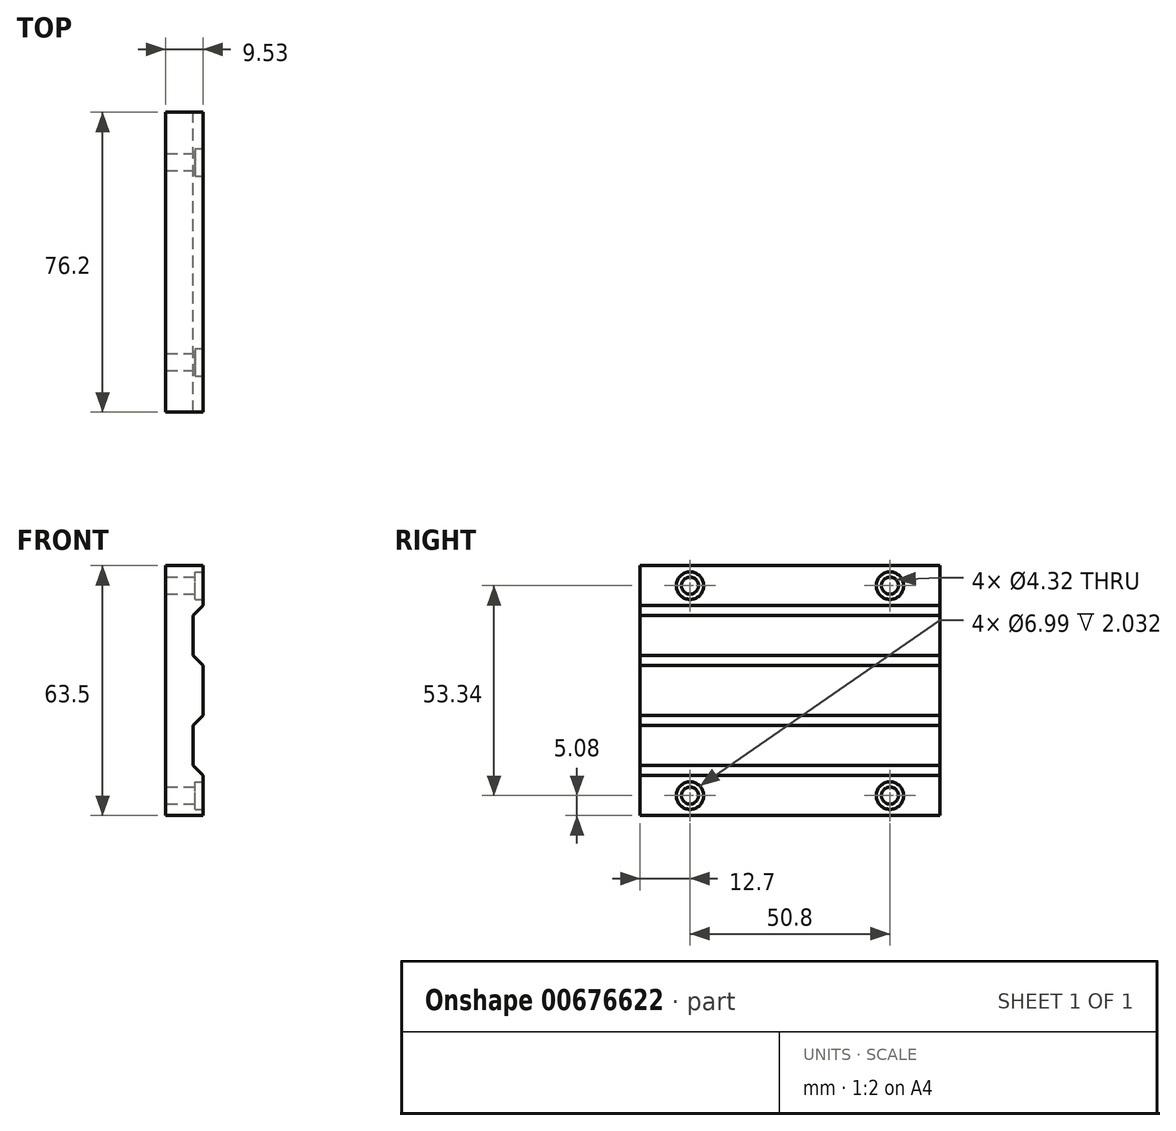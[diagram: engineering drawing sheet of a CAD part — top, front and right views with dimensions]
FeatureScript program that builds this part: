
annotation { "Feature Type Name" : "Feature", "Feature Type Description" : "" }
export const myFeature = defineFeature(function(context is Context, id is Id, definition is map)
    precondition{}
    {
        {
            var Q0;
            Q0=qCreatedBy(makeId("Front.planeOp"),FACE);
            var sketch = newSketch(context, id + "F0", { "sketchPlane" : qUnion([Q0])});
            skLineSegment(sketch, "E0.bottom", {"start": v(0, 0) * mm, "end": v(9.53, 0) * mm});
            skLineSegment(sketch, "E0.top", {"start": v(0, 63.5) * mm, "end": v(9.52, 63.5) * mm});
            skLineSegment(sketch, "E0.left", {"start": v(0, 0) * mm, "end": v(0, 63.5) * mm});
            skLineSegment(sketch, "E0.right", {"start": v(9.53, 0) * mm, "end": v(9.52, 63.5) * mm});
            skPoint(sketch, "E1.endSnap0", {"position": v(4.76, 63.5) * mm});
            skLineSegment(sketch, "E2", {"start": v(6.98, 50.8) * mm, "end": v(6.98, 40.64) * mm});
            skLineSegment(sketch, "E3", {"start": v(6.98, 40.64) * mm, "end": v(9.52, 38.1) * mm});
            skLineSegment(sketch, "E4", {"start": v(9.53, 25.4) * mm, "end": v(6.98, 22.86) * mm});
            skLineSegment(sketch, "E5", {"start": v(6.98, 22.86) * mm, "end": v(6.99, 12.7) * mm});
            skLineSegment(sketch, "E6", {"start": v(6.99, 12.7) * mm, "end": v(9.53, 10.16) * mm});
            skLineSegment(sketch, "E7", {"start": v(6.98, 50.8) * mm, "end": v(9.52, 53.34) * mm});
            skSolve(sketch);
        }
        {
            var Q0;
            {var subQ5=sQuery(id+"F0.wireOp",EDGE,"E0.bottom");Q0=makeQuery(id+"F0.imprint","IMPRINT",FACE,{"disambiguationData":[TD([[makeQuery(id+"F0.imprint","IMPRINT",EDGE,{"derivedFrom":subQ5}),1.0]])]});}
            extrude(context, id + "F1", {"entities" : qUnion([Q0]), "depth" : 76.2 * mm});
        }
        {
            var Q0;
            Q0=makeQuery(id+"F1.opExtrude","CAP_FACE",FACE,{"disambiguationData":[OSD([sQuery(id+"F0.wireOp",EDGE,"E0.bottom"),sQuery(id+"F0.wireOp",EDGE,"E0.top"),sQuery(id+"F0.wireOp",EDGE,"E0.left"),sQuery(id+"F0.wireOp",EDGE,"E0.right"),sQuery(id+"F0.wireOp",EDGE,"E2"),sQuery(id+"F0.wireOp",EDGE,"E3"),sQuery(id+"F0.wireOp",EDGE,"E4"),sQuery(id+"F0.wireOp",EDGE,"E5"),sQuery(id+"F0.wireOp",EDGE,"E6"),sQuery(id+"F0.wireOp",EDGE,"E7")])],"isStart":false});
            var sketch = newSketch(context, id + "F2", { "sketchPlane" : qUnion([Q0])});
            skLineSegment(sketch, "E8.0.0", {"start": v(6.98, 40.64) * mm, "end": v(6.98, 50.8) * mm});
            skLineSegment(sketch, "E8.0.1", {"start": v(6.98, 50.8) * mm, "end": v(9.52, 53.34) * mm});
            skLineSegment(sketch, "E8.0.2", {"start": v(9.52, 53.34) * mm, "end": v(9.52, 63.5) * mm});
            skLineSegment(sketch, "E8.0.3", {"start": v(9.52, 63.5) * mm, "end": v(0, 63.5) * mm});
            skLineSegment(sketch, "E8.0.4", {"start": v(0, 63.5) * mm, "end": v(0, 0) * mm});
            skLineSegment(sketch, "E8.0.5", {"start": v(0, 0) * mm, "end": v(9.53, 0) * mm});
            skLineSegment(sketch, "E8.0.6", {"start": v(9.53, 0) * mm, "end": v(9.53, 10.16) * mm});
            skLineSegment(sketch, "E8.0.7", {"start": v(9.53, 10.16) * mm, "end": v(6.99, 12.7) * mm});
            skLineSegment(sketch, "E8.0.8", {"start": v(6.99, 12.7) * mm, "end": v(6.98, 22.86) * mm});
            skLineSegment(sketch, "E8.0.9", {"start": v(6.98, 22.86) * mm, "end": v(9.53, 25.4) * mm});
            skLineSegment(sketch, "E8.0.10", {"start": v(9.53, 25.4) * mm, "end": v(9.52, 38.1) * mm});
            skLineSegment(sketch, "E8.0.11", {"start": v(9.52, 38.1) * mm, "end": v(6.98, 40.64) * mm});
            skSolve(sketch);
        }
        {
            var Q0;
            {var subQ0=sQuery(id+"F0.wireOp",EDGE,"E0.right");Q0=makeQuery(id+"F1.opExtrude","SWEPT_FACE",FACE,{"disambiguationData":[OSD([subQ0]),TDD([makeQuery(id+"F0.imprint","IMPRINT",EDGE,{"disambiguationData":[TD([[makeQuery(id+"F0.imprint","INTERSECT",VERTEX,{"derivedFrom":[sQuery(id+"F0.wireOp",EDGE,"E0.top"),subQ0]}),1.0]])],"derivedFrom":subQ0})])]});}
            var sketch = newSketch(context, id + "F3", { "sketchPlane" : qUnion([Q0])});
            skPoint(sketch, "E9", {"position": v(-63.5, 58.42) * mm});
            skPoint(sketch, "E9.positionSnap0", {"position": v(-76.2, 58.42) * mm});
            skPoint(sketch, "E10", {"position": v(-12.7, 58.42) * mm});
            skPoint(sketch, "E11", {"position": v(-12.7, 5.08) * mm});
            skPoint(sketch, "E12", {"position": v(-63.5, 5.08) * mm});
            skSolve(sketch);
        }
        {
            var Q0;
            Q0=sQuery(id+"F3.wireOp",VERTEX,"E9");
            var Q1;
            Q1=sQuery(id+"F3.wireOp",VERTEX,"E10");
            var Q2;
            Q2=sQuery(id+"F3.wireOp",VERTEX,"E12");
            var Q3;
            Q3=sQuery(id+"F3.wireOp",VERTEX,"E11");
            var Q4;
            Q4=makeQuery(id+"F1.opExtrude","SWEPT_BODY",BODY,{"disambiguationData":[OSD([sQuery(id+"F0.wireOp",EDGE,"E0.bottom"),sQuery(id+"F0.wireOp",EDGE,"E0.top"),sQuery(id+"F0.wireOp",EDGE,"E0.left"),sQuery(id+"F0.wireOp",EDGE,"E0.right"),sQuery(id+"F0.wireOp",EDGE,"E2"),sQuery(id+"F0.wireOp",EDGE,"E3"),sQuery(id+"F0.wireOp",EDGE,"E4"),sQuery(id+"F0.wireOp",EDGE,"E5"),sQuery(id+"F0.wireOp",EDGE,"E6"),sQuery(id+"F0.wireOp",EDGE,"E7")])]});
            hole(context, id + "F4", {"style" : HoleStyle.SIMPLE, "endStyle" : HoleEndStyle.BLIND, "standardTappedOrClearance" : lookupTablePath({ "standard" : "ANSI", "fit" : "Close", "size" : "#8", "type" : "Clearance" }), "standardBlindInLast" : lookupTablePath({ "fit" : "Close", "standard" : "ANSI", "size" : "#8", "type" : "Clearance" }), "holeDiameter" : 4.32 * mm, "holeDepth" : 12.7 * mm, "isTappedThrough" : true, "tappedDepth" : 10.32 * mm, "tapClearance" : 3, "locations" : qUnion([Q0, Q1, Q2, Q3]), "scope" : qUnion([Q4])});
        }
        {
            var Q0;
            {var subQ0=sQuery(id+"F0.wireOp",EDGE,"E0.right");Q0=makeQuery(id+"F1.opExtrude","SWEPT_FACE",FACE,{"disambiguationData":[OSD([subQ0]),TDD([makeQuery(id+"F0.imprint","IMPRINT",EDGE,{"disambiguationData":[TD([[makeQuery(id+"F0.imprint","INTERSECT",VERTEX,{"derivedFrom":[sQuery(id+"F0.wireOp",EDGE,"E0.top"),subQ0]}),1.0]])],"derivedFrom":subQ0})])]});}
            var sketch = newSketch(context, id + "F5", { "sketchPlane" : qUnion([Q0])});
            skCircle(sketch, "E13", {"center": v(-63.5, 58.42) * mm, "radius": 3.5 * mm});
            skCircle(sketch, "E14", {"center": v(-12.7, 58.42) * mm, "radius": 3.5 * mm});
            skLineSegment(sketch, "E15.0.0", {"start": v(0, 0) * mm, "end": v(0, 10.16) * mm});
            skLineSegment(sketch, "E15.0.1", {"start": v(0, 10.16) * mm, "end": v(-76.2, 10.16) * mm});
            skLineSegment(sketch, "E15.0.2", {"start": v(-76.2, 10.16) * mm, "end": v(-76.2, 0) * mm});
            skLineSegment(sketch, "E15.0.3", {"start": v(-76.2, 0) * mm, "end": v(0, 0) * mm});
            skCircle(sketch, "E16.0", {"center": v(-63.5, 5.08) * mm, "radius": 2.16 * mm});
            skCircle(sketch, "E17.0", {"center": v(-12.7, 5.08) * mm, "radius": 2.16 * mm});
            skCircle(sketch, "E18", {"center": v(-63.5, 5.08) * mm, "radius": 3.5 * mm});
            skCircle(sketch, "E19", {"center": v(-12.7, 5.08) * mm, "radius": 3.5 * mm});
            skSolve(sketch);
        }
        {
            var Q0;
            Q0=makeQuery(id+"F5.imprint","IMPRINT",FACE,{"disambiguationData":[TD([[makeQuery(id+"F5.imprint","IMPRINT",EDGE,{"derivedFrom":sQuery(id+"F5.wireOp",EDGE,"E13")}),1.0]])]});
            var Q1;
            Q1=makeQuery(id+"F5.imprint","IMPRINT",FACE,{"disambiguationData":[TD([[makeQuery(id+"F5.imprint","IMPRINT",EDGE,{"derivedFrom":sQuery(id+"F5.wireOp",EDGE,"E14")}),1.0]])]});
            var Q2;
            Q2=makeQuery(id+"F5.imprint","IMPRINT",FACE,{"disambiguationData":[TD([[makeQuery(id+"F5.imprint","IMPRINT",EDGE,{"derivedFrom":sQuery(id+"F5.wireOp",EDGE,"E16.0")}),-1.0]])]});
            var Q3;
            Q3=makeQuery(id+"F5.imprint","IMPRINT",FACE,{"disambiguationData":[TD([[makeQuery(id+"F5.imprint","IMPRINT",EDGE,{"derivedFrom":sQuery(id+"F5.wireOp",EDGE,"E17.0")}),-1.0]])]});
            extrude(context, id + "F6", {"entities" : qUnion([Q0, Q1, Q2, Q3]), "operationType" : NewBodyOperationType.REMOVE, "oppositeDirection" : true, "depth" : 2.03 * mm});
        }
    });
